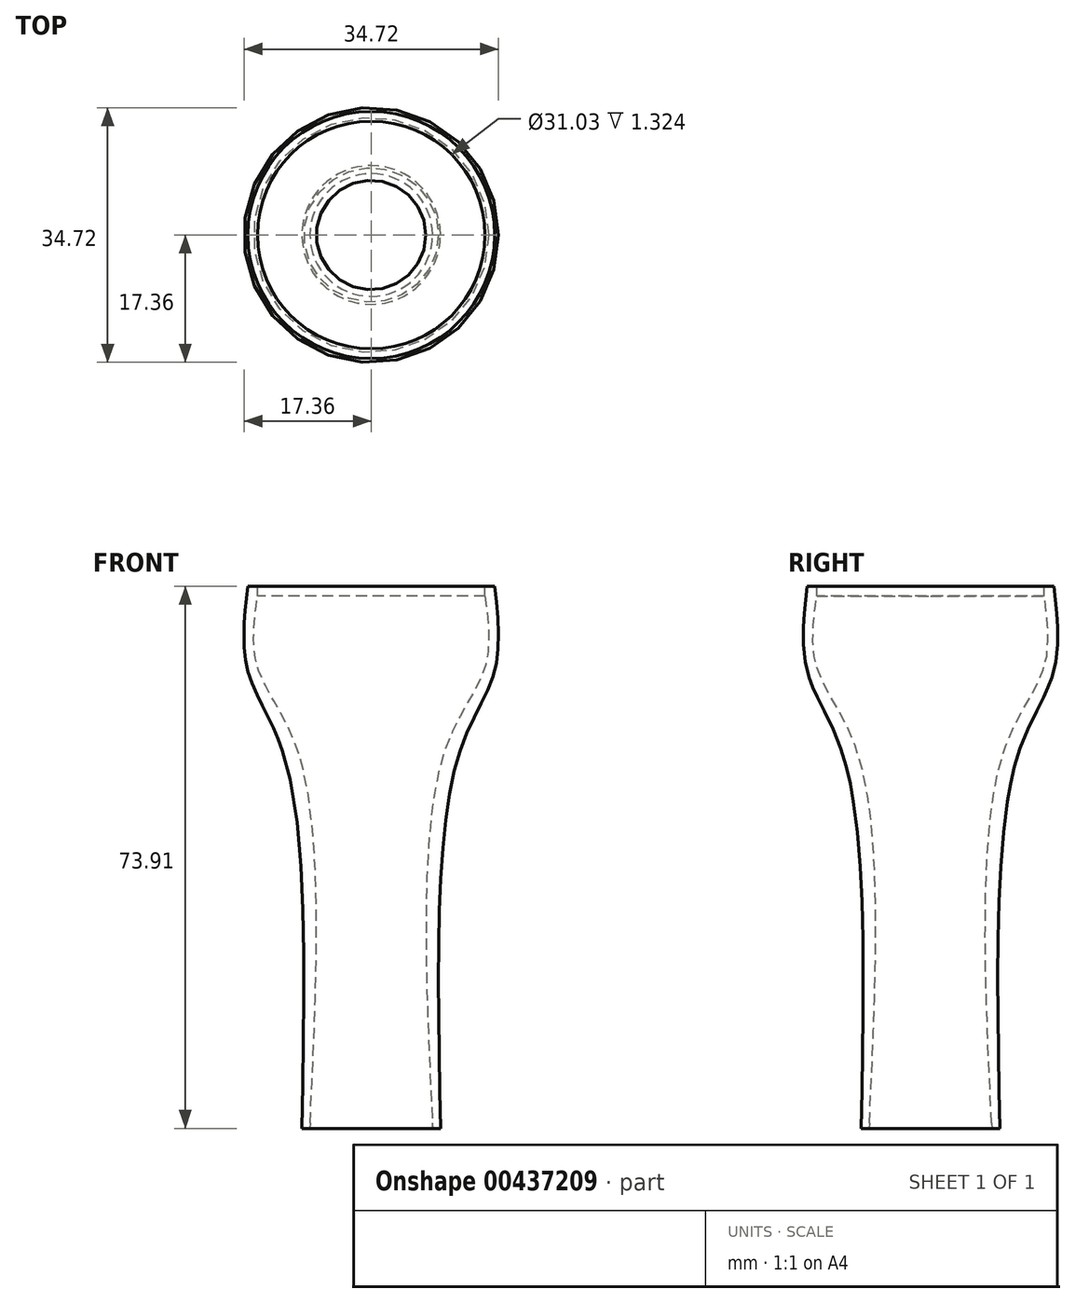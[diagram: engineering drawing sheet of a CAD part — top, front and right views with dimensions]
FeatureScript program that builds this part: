
annotation { "Feature Type Name" : "Feature", "Feature Type Description" : "" }
export const myFeature = defineFeature(function(context is Context, id is Id, definition is map)
    precondition{}
    {
        {
            var Q0;
            Q0=qCreatedBy(makeId("Front.planeOp"),FACE);
            var sketch = newSketch(context, id + "F0", { "sketchPlane" : qUnion([Q0])});
            skLineSegment(sketch, "E0", {"start": v(0, 0.72) * mm, "end": v(0, -20.4) * mm, "construction": true});
            skLineSegment(sketch, "E1", {"start": v(15.52, 73.9) * mm, "end": v(16.83, 73.9) * mm});
            skFitSpline(sketch, "E2", {"points": [v(16.83, 73.9) * mm, v(16.83, 62.38) * mm, v(11.76, 50.39) * mm, v(9.45, 0) * mm], "startDerivative": vector(5.68, -50.43) * mm, "endDerivative": vector(2.48, -118.6) * mm});
            skLineSegment(sketch, "E3", {"start": v(9.45, 0) * mm, "end": v(0, 0) * mm});
            skLineSegment(sketch, "E4", {"start": v(0, 0.72) * mm, "end": v(0, 0) * mm});
            skFitSpline(sketch, "E5", {"points": [v(15.52, 72.58) * mm, v(15.52, 62.9) * mm, v(9.87, 51.02) * mm, v(8.37, 0) * mm], "startDerivative": vector(6, -44.85) * mm, "endDerivative": vector(5.61, -117.58) * mm});
            skLineSegment(sketch, "E6", {"start": v(0, 0.72) * mm, "end": v(8.33, 0.72) * mm});
            skLineSegment(sketch, "E7", {"start": v(15.52, 72.58) * mm, "end": v(15.52, 73.9) * mm});
            skPoint(sketch, "E8.orphan", {"position": v(0, 73.9) * mm});
            skSolve(sketch);
        }
        {
            var Q0;
            Q0=makeQuery(id+"F0.imprint","IMPRINT",FACE,{"disambiguationData":[TD([[makeQuery(id+"F0.imprint","IMPRINT",EDGE,{"derivedFrom":sQuery(id+"F0.wireOp",EDGE,"E1")}),-1.0]])]});
            var Q1;
            Q1=sQuery(id+"F0.wireOp",EDGE,"E0");
            revolve(context, id + "F1", {"entities" : qUnion([Q0]), "axis" : qUnion([Q1]), "revolveType" : RevolveType.FULL});
        }
    });
